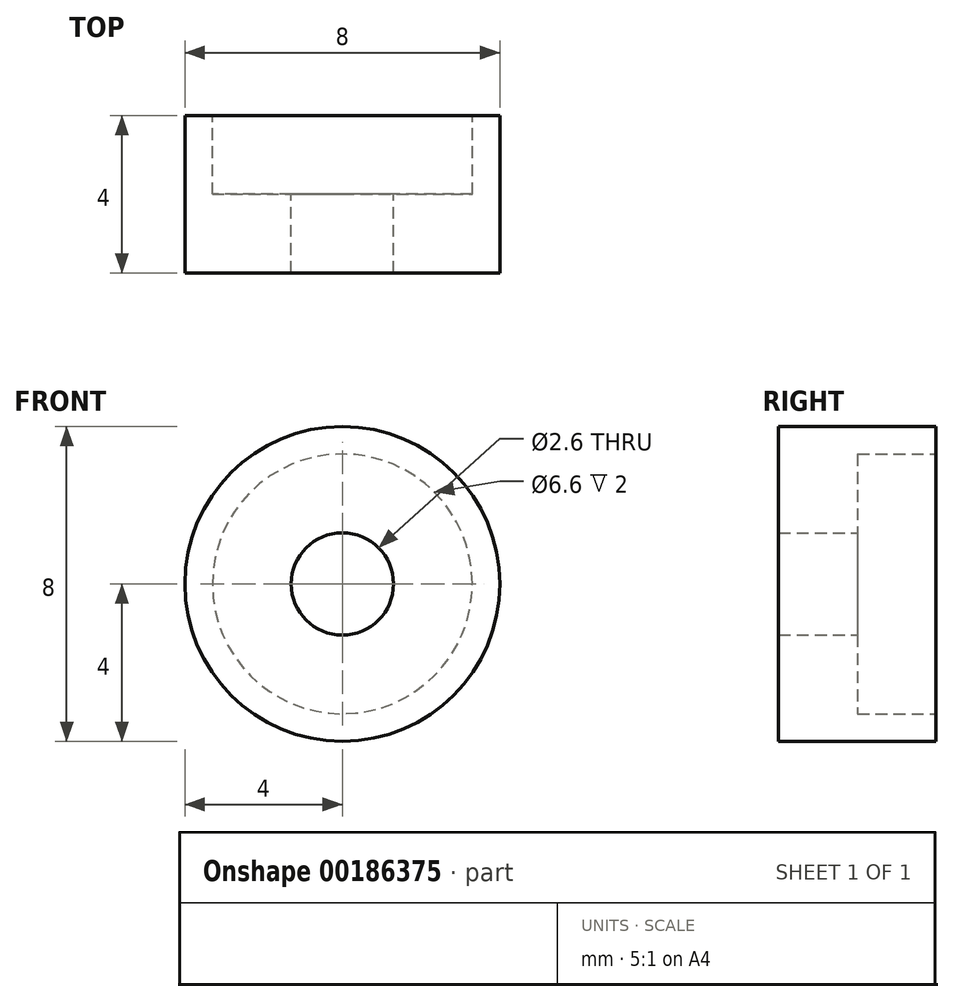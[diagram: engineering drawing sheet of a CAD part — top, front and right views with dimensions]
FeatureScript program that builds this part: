
annotation { "Feature Type Name" : "Feature", "Feature Type Description" : "" }
export const myFeature = defineFeature(function(context is Context, id is Id, definition is map)
    precondition{}
    {
        {
            var Q0;
            Q0=qCreatedBy(makeId("Right.planeOp"),FACE);
            var sketch = newSketch(context, id + "F0", { "sketchPlane" : qUnion([Q0])});
            skLineSegment(sketch, "E0", {"start": v(11.47, 0) * mm, "end": v(0, 0) * mm, "construction": true});
            skLineSegment(sketch, "E1", {"start": v(2, 1.3) * mm, "end": v(0, 1.3) * mm});
            skLineSegment(sketch, "E2", {"start": v(2, 1.3) * mm, "end": v(2, 3.3) * mm});
            skLineSegment(sketch, "E3", {"start": v(4, 3.3) * mm, "end": v(2, 3.3) * mm});
            skLineSegment(sketch, "E4", {"start": v(4, 3.3) * mm, "end": v(4, 4) * mm});
            skLineSegment(sketch, "E5", {"start": v(0, 4) * mm, "end": v(4, 4) * mm});
            skLineSegment(sketch, "E6", {"start": v(0, 0) * mm, "end": v(0, 4) * mm});
            skLineSegment(sketch, "E7", {"start": v(0, 0) * mm, "end": v(0, 0) * mm});
            skLineSegment(sketch, "E8", {"start": v(0, 1.3) * mm, "end": v(0, 0) * mm});
            skSolve(sketch);
        }
        {
            var Q0;
            Q0=makeQuery(id+"F0.imprint","IMPRINT",FACE,{"disambiguationData":[TD([[makeQuery(id+"F0.imprint","IMPRINT",EDGE,{"derivedFrom":sQuery(id+"F0.wireOp",EDGE,"E1")}),-1.0]])]});
            var Q1;
            Q1=sQuery(id+"F0.wireOp",EDGE,"E0");
            revolve(context, id + "F1", {"entities" : qUnion([Q0]), "axis" : qUnion([Q1]), "revolveType" : RevolveType.FULL});
        }
    });
